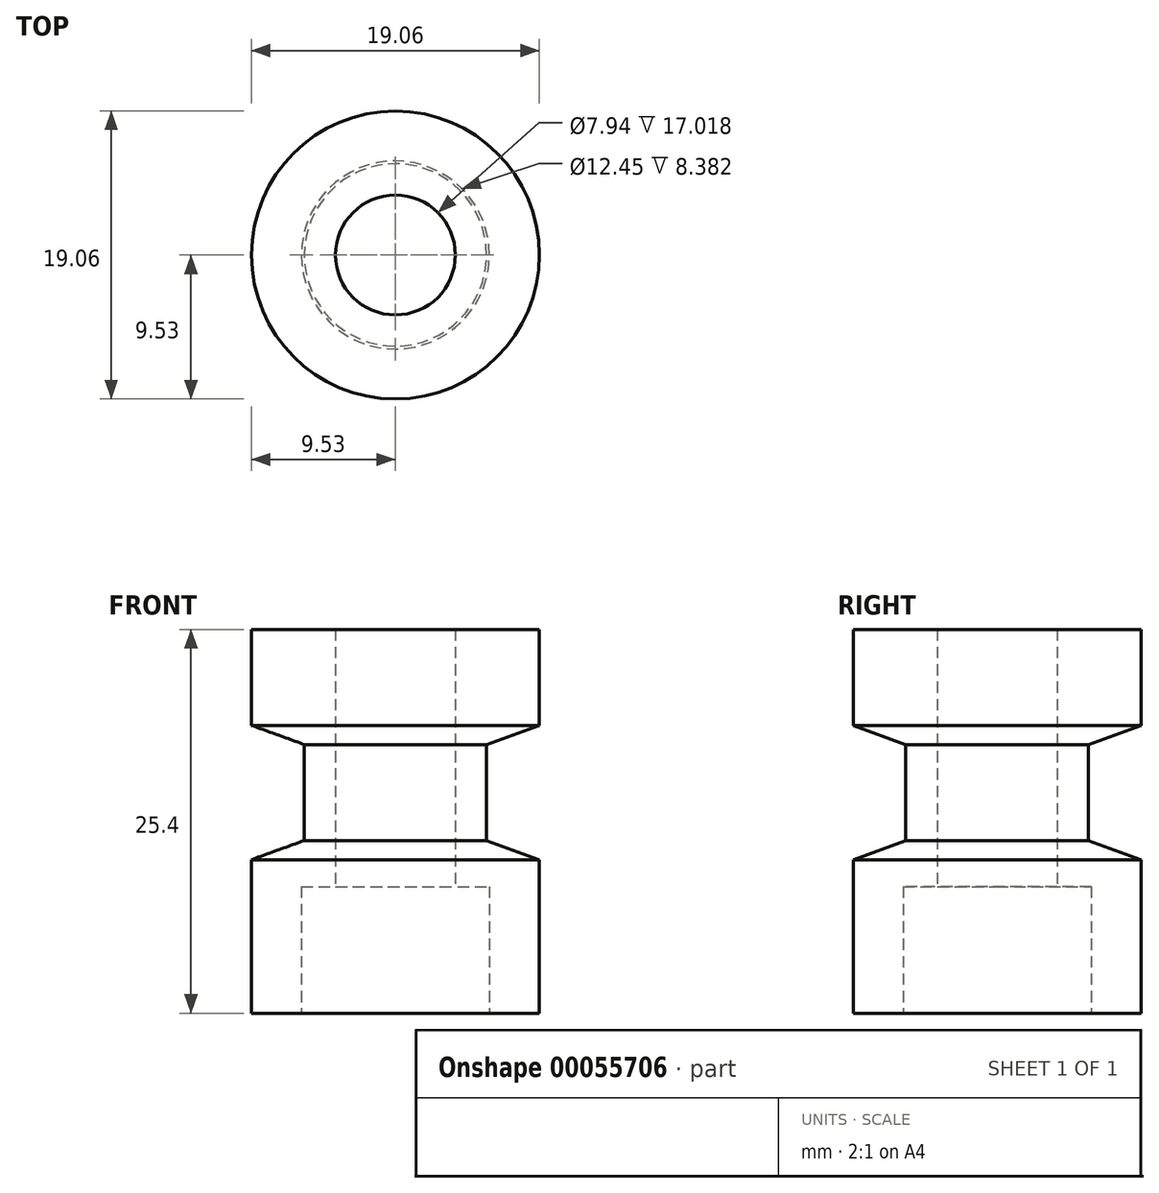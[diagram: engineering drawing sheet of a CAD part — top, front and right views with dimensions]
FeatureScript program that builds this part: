
annotation { "Feature Type Name" : "Feature", "Feature Type Description" : "" }
export const myFeature = defineFeature(function(context is Context, id is Id, definition is map)
    precondition{}
    {
        {
            var Q0;
            Q0=qCreatedBy(makeId("Front.planeOp"),FACE);
            var sketch = newSketch(context, id + "F0", { "sketchPlane" : qUnion([Q0])});
            skLineSegment(sketch, "E0", {"start": v(0, 0) * mm, "end": v(0, 12.7) * mm});
            skLineSegment(sketch, "E1", {"start": v(0, 0) * mm, "end": v(0, -12.7) * mm});
            skLineSegment(sketch, "E2", {"start": v(0, 12.7) * mm, "end": v(9.53, 12.7) * mm});
            skLineSegment(sketch, "E3", {"start": v(9.52, 12.7) * mm, "end": v(9.52, 6.35) * mm});
            skLineSegment(sketch, "E4", {"start": v(9.52, 6.35) * mm, "end": v(6.04, 5.08) * mm});
            skLineSegment(sketch, "E5", {"start": v(6.04, 5.08) * mm, "end": v(6.04, -1.27) * mm});
            skLineSegment(sketch, "E6", {"start": v(6.04, -1.27) * mm, "end": v(9.52, -2.54) * mm});
            skLineSegment(sketch, "E7", {"start": v(9.52, -2.54) * mm, "end": v(9.52, -12.7) * mm});
            skLineSegment(sketch, "E8", {"start": v(9.53, -12.7) * mm, "end": v(0, -12.7) * mm});
            skLineSegment(sketch, "E9", {"start": v(0, -18.57) * mm, "end": v(0, 23.18) * mm, "construction": true});
            skSolve(sketch);
        }
        {
            var Q0;
            Q0=makeQuery(id+"F0.imprint","IMPRINT",FACE,{"disambiguationData":[TD([[makeQuery(id+"F0.imprint","IMPRINT",EDGE,{"derivedFrom":sQuery(id+"F0.wireOp",EDGE,"E0")}),-1.0]])]});
            var Q1;
            Q1=sQuery(id+"F0.wireOp",EDGE,"E9");
            var Q2;
            Q2=sQuery(id+"F0.wireOp",EDGE,"E9");
            revolve(context, id + "F1", {"entities" : qUnion([Q0]), "surfaceEntities" : qUnion([Q1]), "axis" : qUnion([Q2]), "revolveType" : RevolveType.FULL});
        }
        {
            var Q0;
            Q0=makeQuery(id+"F1.opRevolve","SWEPT_FACE",FACE,{"disambiguationData":[OSD([sQuery(id+"F0.wireOp",EDGE,"E8")])]});
            var sketch = newSketch(context, id + "F2", { "sketchPlane" : qUnion([Q0])});
            skCircle(sketch, "E10", {"center": v(0, 0) * mm, "radius": 3.97 * mm});
            skSolve(sketch);
        }
        {
            var Q0;
            Q0=makeQuery(id+"F2.imprint","IMPRINT",FACE,{"disambiguationData":[TD([[makeQuery(id+"F2.imprint","IMPRINT",EDGE,{"derivedFrom":sQuery(id+"F2.wireOp",EDGE,"ccc328a1-0efb-4503-9499-4143a87ccc20")}),1.0]])]});
            var Q1;
            Q1=makeQuery(id+"F2.imprint","IMPRINT",FACE,{"disambiguationData":[TD([[makeQuery(id+"F2.imprint","IMPRINT",EDGE,{"derivedFrom":sQuery(id+"F2.wireOp",EDGE,"E10")}),1.0]])]});
            extrude(context, id + "F3", {"entities" : qUnion([Q0, Q1]), "operationType" : NewBodyOperationType.REMOVE, "endBound" : BoundingType.THROUGH_ALL, "oppositeDirection" : true, "depth" : 25.4 * mm});
        }
        {
            var Q0;
            Q0=makeQuery(id+"F1.opRevolve","SWEPT_FACE",FACE,{"disambiguationData":[OSD([sQuery(id+"F0.wireOp",EDGE,"E8")])]});
            var sketch = newSketch(context, id + "F4", { "sketchPlane" : qUnion([Q0])});
            skCircle(sketch, "E11", {"center": v(0, 0) * mm, "radius": 6.22 * mm});
            skSolve(sketch);
        }
        {
            var Q0;
            Q0=makeQuery(id+"F4.imprint","IMPRINT",FACE,{"disambiguationData":[TD([[makeQuery(id+"F4.imprint","IMPRINT",EDGE,{"derivedFrom":sQuery(id+"F4.wireOp",EDGE,"E11")}),1.0]])]});
            extrude(context, id + "F5", {"entities" : qUnion([Q0]), "operationType" : NewBodyOperationType.REMOVE, "oppositeDirection" : true, "depth" : 8.38 * mm});
        }
    });
